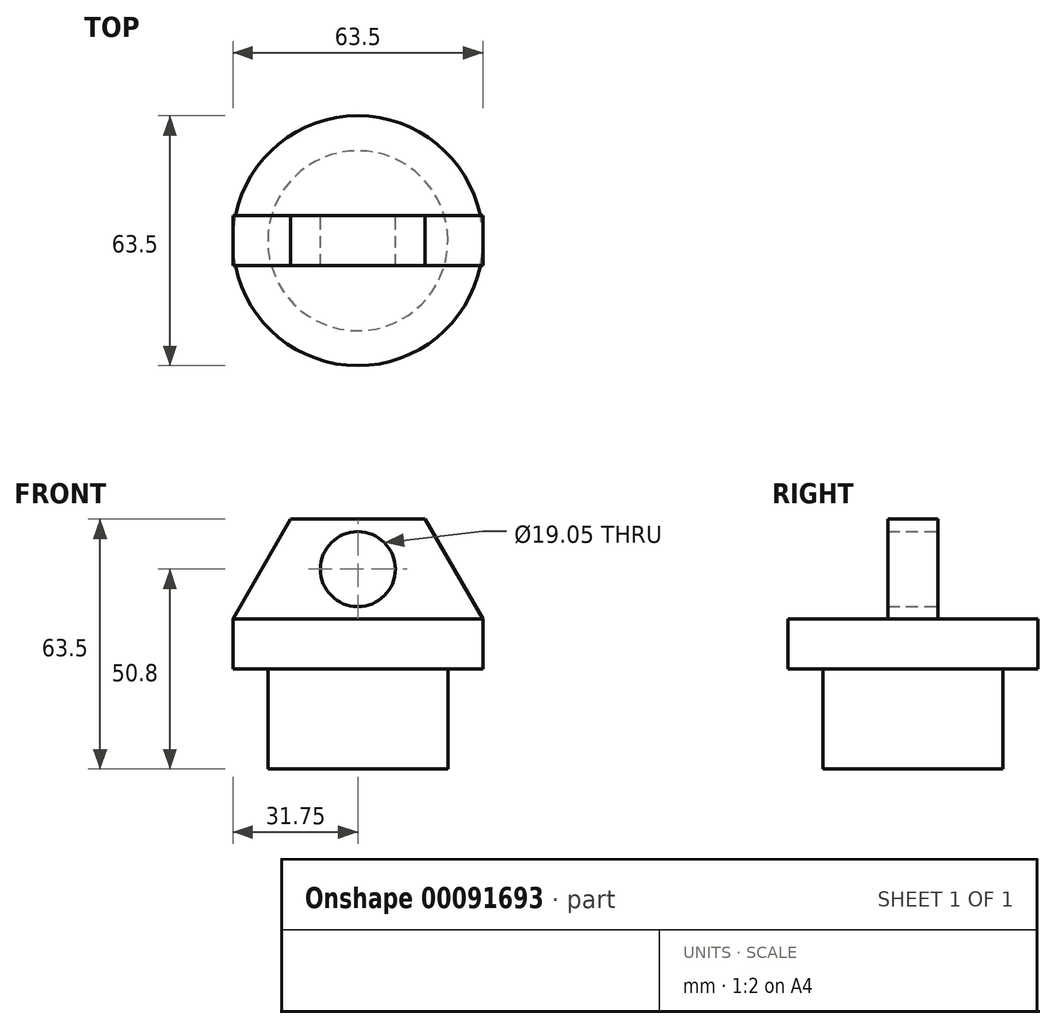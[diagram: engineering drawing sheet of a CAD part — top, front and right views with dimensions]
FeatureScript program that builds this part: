
annotation { "Feature Type Name" : "Feature", "Feature Type Description" : "" }
export const myFeature = defineFeature(function(context is Context, id is Id, definition is map)
    precondition{}
    {
        {
            var Q0;
            Q0=qCreatedBy(makeId("Top.planeOp"),FACE);
            var sketch = newSketch(context, id + "F0", { "sketchPlane" : qUnion([Q0])});
            skCircle(sketch, "E0", {"center": v(0, 0) * mm, "radius": 22.86 * mm});
            skSolve(sketch);
        }
        {
            var Q0;
            Q0 = qSketchRegion(id + "F0", true);
            extrude(context, id + "F1", {"entities" : qUnion([Q0]), "depth" : 25.4 * mm});
        }
        {
            var Q0;
            Q0=makeQuery(id+"F1.opExtrude","CAP_FACE",FACE,{"disambiguationData":[OSD([sQuery(id+"F0.wireOp",EDGE,"E0")])],"isStart":false});
            var sketch = newSketch(context, id + "F2", { "sketchPlane" : qUnion([Q0])});
            skCircle(sketch, "E1", {"center": v(0, 0) * mm, "radius": 31.75 * mm});
            skSolve(sketch);
        }
        {
            var Q0;
            Q0 = qSketchRegion(id + "F2", true);
            extrude(context, id + "F3", {"entities" : qUnion([Q0]), "operationType" : NewBodyOperationType.ADD, "depth" : 12.7 * mm});
        }
        {
            var Q0;
            Q0=qCreatedBy(makeId("Front.planeOp"),FACE);
            var sketch = newSketch(context, id + "F4", { "sketchPlane" : qUnion([Q0])});
            skLineSegment(sketch, "E2", {"start": v(0, 38.1) * mm, "end": v(-31.75, 38.1) * mm});
            skLineSegment(sketch, "E3", {"start": v(-31.75, 38.1) * mm, "end": v(-17.09, 63.5) * mm});
            skLineSegment(sketch, "E4", {"start": v(-17.09, 63.5) * mm, "end": v(0, 63.5) * mm});
            skLineSegment(sketch, "E5", {"start": v(0, 38.1) * mm, "end": v(0, 63.5) * mm, "construction": true});
            skLineSegment(sketch, "E6.MirrorCS", {"start": v(0, 38.1) * mm, "end": v(31.75, 38.1) * mm});
            skLineSegment(sketch, "E7.MirrorCS", {"start": v(31.75, 38.1) * mm, "end": v(17.09, 63.5) * mm});
            skLineSegment(sketch, "E8.MirrorCS", {"start": v(17.09, 63.5) * mm, "end": v(0, 63.5) * mm});
            skCircle(sketch, "E9", {"center": v(0, 50.8) * mm, "radius": 9.53 * mm});
            skSolve(sketch);
        }
        {
            var Q0;
            Q0 = qSketchRegion(id + "F4", true);
            extrude(context, id + "F5", {"entities" : qUnion([Q0]), "operationType" : NewBodyOperationType.ADD, "endBound" : BoundingType.SYMMETRIC, "depth" : 12.7 * mm});
        }
    });
